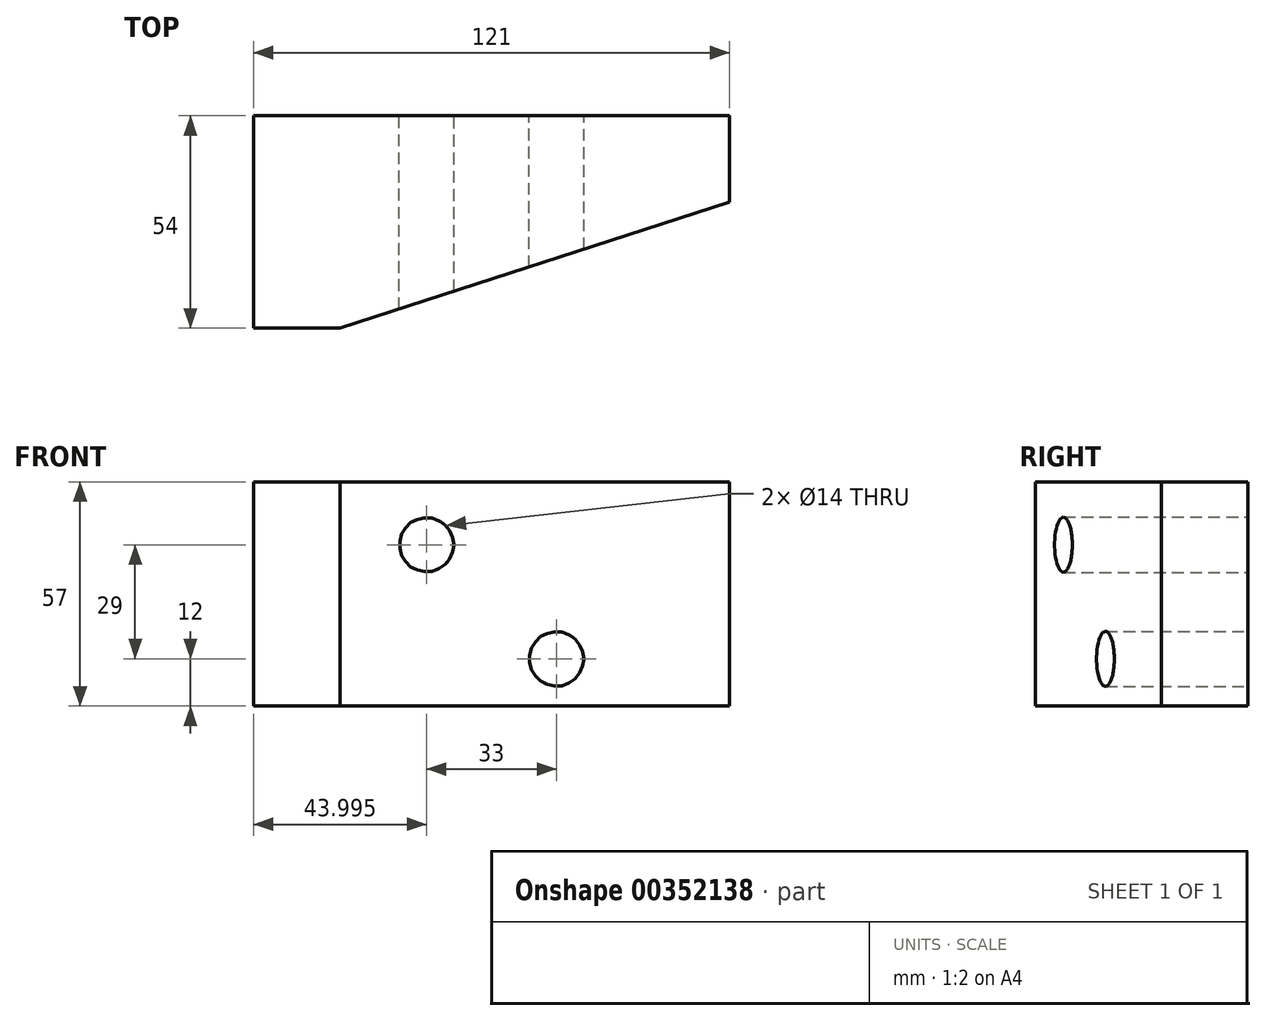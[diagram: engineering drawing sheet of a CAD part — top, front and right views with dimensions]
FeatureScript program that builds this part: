
annotation { "Feature Type Name" : "Feature", "Feature Type Description" : "" }
export const myFeature = defineFeature(function(context is Context, id is Id, definition is map)
    precondition{}
    {
        {
            var Q0;
            Q0=qCreatedBy(makeId("Front.planeOp"),FACE);
            var sketch = newSketch(context, id + "F0", { "sketchPlane" : qUnion([Q0])});
            skLineSegment(sketch, "E0", {"start": v(-52.65, 57) * mm, "end": v(-52.65, 0) * mm});
            skLineSegment(sketch, "E1", {"start": v(-52.65, 0) * mm, "end": v(68.35, 0) * mm});
            skLineSegment(sketch, "E2", {"start": v(68.35, 0) * mm, "end": v(68.35, 57) * mm});
            skLineSegment(sketch, "E3", {"start": v(68.35, 57) * mm, "end": v(-52.65, 57) * mm});
            skLineSegment(sketch, "E4", {"start": v(-52.65, 46) * mm, "end": v(6.35, 0) * mm});
            skLineSegment(sketch, "E5", {"start": v(9.35, 57) * mm, "end": v(68.35, 11) * mm});
            skPoint(sketch, "E6", {"position": v(-8.65, 41) * mm});
            skPoint(sketch, "E7", {"position": v(24.35, 12) * mm});
            skLineSegment(sketch, "E8", {"start": v(-30.65, 28.85) * mm, "end": v(-30.65, 0) * mm});
            skCircle(sketch, "E9", {"center": v(-8.65, 41) * mm, "radius": 7 * mm});
            skCircle(sketch, "E10", {"center": v(24.35, 12) * mm, "radius": 7 * mm});
            skSolve(sketch);
        }
        {
            var Q0;
            Q0 = qSketchRegion(id + "F0", true);
            extrude(context, id + "F1", {"entities" : qUnion([Q0]), "depth" : 54 * mm});
        }
        {
            var Q0;
            Q0=makeQuery(id+"F1.opExtrude","SWEPT_FACE",FACE,{"disambiguationData":[OSD([sQuery(id+"F0.wireOp",EDGE,"E3")])]});
            var sketch = newSketch(context, id + "F2", { "sketchPlane" : qUnion([Q0])});
            skLineSegment(sketch, "E11", {"start": v(-52.65, -54) * mm, "end": v(-30.65, -54) * mm});
            skLineSegment(sketch, "E12", {"start": v(-30.65, -54) * mm, "end": v(68.35, -22) * mm});
            skLineSegment(sketch, "E13", {"start": v(68.35, 0) * mm, "end": v(-52.65, 0) * mm});
            skLineSegment(sketch, "E14", {"start": v(-52.65, 0) * mm, "end": v(-52.65, -54) * mm});
            skLineSegment(sketch, "E15", {"start": v(78.94, -16) * mm, "end": v(-15.3, -16) * mm, "construction": true});
            skLineSegment(sketch, "E16", {"start": v(68.35, 0) * mm, "end": v(68.35, -22) * mm});
            skSolve(sketch);
        }
        {
            var Q0;
            {var subQ0=sQuery(id+"F2.wireOp",EDGE,"E12");Q0=makeQuery(id+"F2.imprint","IMPRINT",FACE,{"disambiguationData":[TD([[makeQuery(id+"F2.imprint","IMPRINT",EDGE,{"derivedFrom":subQ0}),-1.0]])]});}
            extrude(context, id + "F3", {"entities" : qUnion([Q0]), "operationType" : NewBodyOperationType.REMOVE, "endBound" : BoundingType.THROUGH_ALL, "oppositeDirection" : true, "depth" : 25 * mm});
        }
    });
